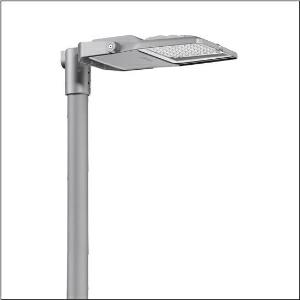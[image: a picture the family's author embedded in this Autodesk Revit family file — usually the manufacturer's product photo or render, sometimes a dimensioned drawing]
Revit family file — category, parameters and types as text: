
# Revit family: floodlight_fl_21_mini___pl61_5xa7775d2c3a_f3a4
name_source: partatom
category: Lighting Fixtures
units: mm (PartAtom-declared; Revit-internal decimal feet)

## family parameters
Cut with Voids When Loaded = No
Host = Face
Light Source = No
Part Type = Normal
Room Calculation Point = No
Round Connector Dimension = Use Diameter
Shared = No

## types (1)
- --- (1 x LED, 17510 lm, 142.9 W, 3000K)
    Apparent Load = 143 VA
    CIE Flux Codes = 33 65 98 100 100
    Color Rendering = 70
    Color Temperature = 3000K
    Default Elevation = 1800 mm
    Description = Floodlight FL 21 mini, floodlight, primary light control with lens, of PMMA, primary optical cover: protective disc, of toughened safety glass, transparent, light distribution: PL61, light emission: direct distribution, installation type: surface-mounted, LED, High Power LED, rated luminous flux: 17.510lm, luminous efficacy: 123lm/W, light colour: 730, colour temperature: 3000K, control: flexible luminous flux parameterisation, time-dependent luminous flux control, constant luminous flux control, overheat protection, presetting dimming logarithmic, with terminal, 6-pole, mains connection: 220..240V, AC, 50/60Hz, start of lifetime: 143W, end of service life: 151W, reduction: 63W, luminaire housing, of diecast aluminium, powder-coated, Siteco® metallic grey (DB 702S), corrosivity category C5 mid according to DIN EN ISO 12944, sealing non-destructively replaceable, please order mast flange separately, mast bracket, of steel, galvanised, powder-coated, Siteco® metallic grey (DB 702S), Smart Interface above, protection rating (complete): IP66, insulation class (complete): insulation class II (safety insulation), certification: CE, ENEC, VDE, protection symbol: D, impact resistance: IK08, permissible operating ambient temperature: -40..+40°C, permissible operating ambient temperature for outdoor applications: -40..+50°C, standard: DIN EN 12944, LABS conformity tested according to VDMA 24364:2018-05, packaging unit: 1 piece

Light Distribution: PL61
    Height = 70 mm
    Lamp = 1 x LED
    Lamp Light Flux = 17510 lm
    Lamp Power = 142.9 W
    Lamp count = 1
    Length = 485 mm
    Luminous efficacy = 123 lm/W
    Manufacturer = Siteco
    ModVariant = No
    Model = 5XA7775D2C3A
    Number of Poles = 1
    OnlyDefault = Yes
    Power Factor = 1
    Product Name = Floodlight FL 21 mini | PL61
    Product group = floodlight | pylon annexe
    ProductGroupID = 6200
    Protection Class = Protection class II
    Protection Degree = IP 66
    RLX_Detail_Level = 1
    RLX_Emergency_Light_Flux = 0 lm
    RLX_Emergency_Type = 0
    RLX_Emergency_Type_DB = No
    RlxData = <blob elided: 101309 chars, md5=ae7753b9>
    Socket = socket
    Standby Power = 0 W
    System Light Flux = 17510 lm
    System Power = 143 W
    Type Comments = factory setting: luminous flux: 100 % | dim-lin: 254 | 730 mA
    Type Image = l_1007125.jpg
    URL = http://relux.com
    VarID = @adj_105001
    Voltage = 0 V
    Weight = 0.00 kg
    Width = 337 mm

## geometry (parser evidence)
native form markers: Blend x4, Sweep x13
no freeform markers — native parametric forms only
